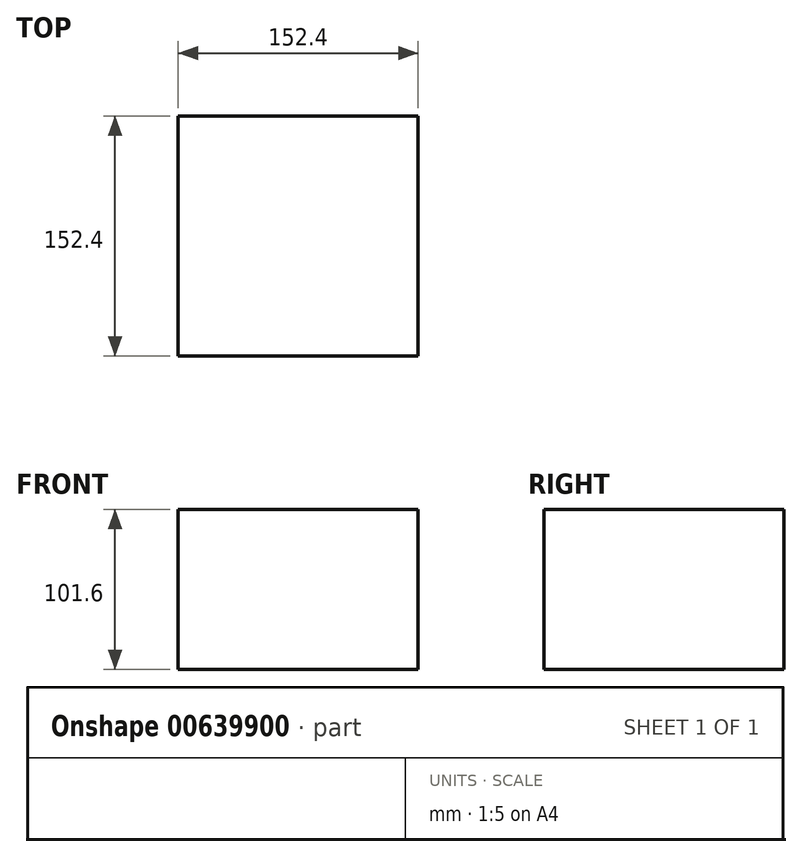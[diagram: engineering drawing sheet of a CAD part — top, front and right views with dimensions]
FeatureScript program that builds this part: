
annotation { "Feature Type Name" : "Feature", "Feature Type Description" : "" }
export const myFeature = defineFeature(function(context is Context, id is Id, definition is map)
    precondition{}
    {
        {
            var Q0;
            Q0=qCreatedBy(makeId("Front.planeOp"),FACE);
            var sketch = newSketch(context, id + "F0", { "sketchPlane" : qUnion([Q0])});
            skLineSegment(sketch, "E0", {"start": v(0, 0) * mm, "end": v(152.4, 0) * mm});
            skLineSegment(sketch, "E1", {"start": v(152.4, 0) * mm, "end": v(152.4, 101.6) * mm});
            skLineSegment(sketch, "E2", {"start": v(152.4, 101.6) * mm, "end": v(0, 101.6) * mm});
            skLineSegment(sketch, "E3", {"start": v(0, 101.6) * mm, "end": v(0, 0) * mm});
            skSolve(sketch);
        }
        {
            var Q0;
            Q0=makeQuery(id+"F0.imprint","IMPRINT",FACE,{"disambiguationData":[TD([[makeQuery(id+"F0.imprint","IMPRINT",EDGE,{"derivedFrom":sQuery(id+"F0.wireOp",EDGE,"E0")}),1.0]])]});
            extrude(context, id + "F1", {"entities" : qUnion([Q0]), "oppositeDirection" : true, "depth" : 152.4 * mm, "offsetDistance" : 25.4 * mm});
        }
    });
